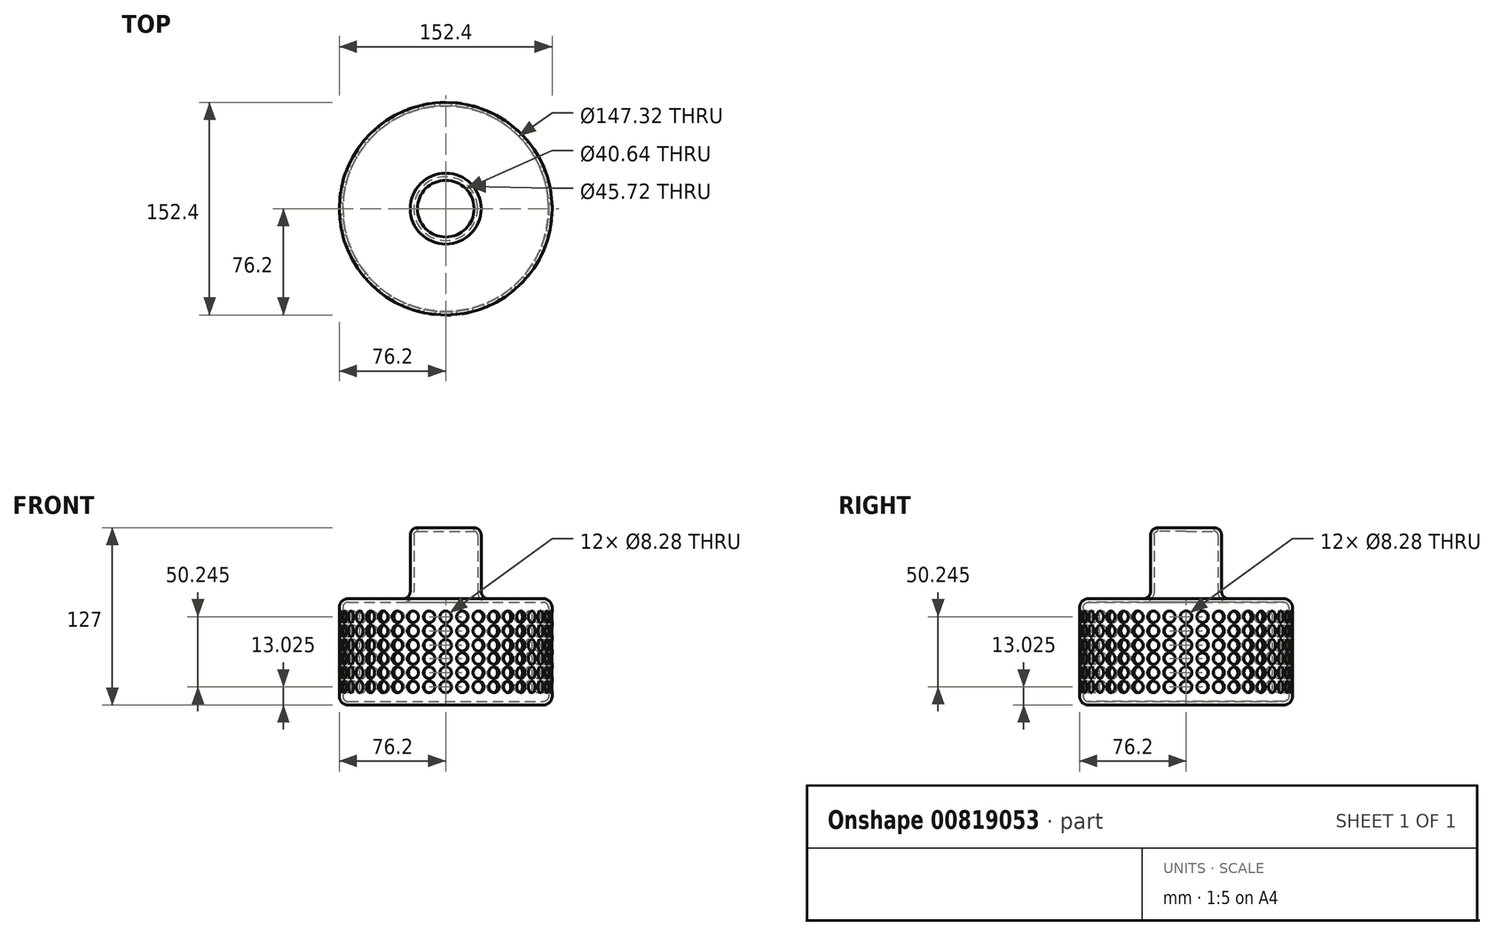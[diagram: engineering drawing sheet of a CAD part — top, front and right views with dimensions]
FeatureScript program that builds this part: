
annotation { "Feature Type Name" : "Feature", "Feature Type Description" : "" }
export const myFeature = defineFeature(function(context is Context, id is Id, definition is map)
    precondition{}
    {
        {
            var Q0;
            Q0=qCreatedBy(makeId("Front.planeOp"),FACE);
            var sketch = newSketch(context, id + "F0", { "sketchPlane" : qUnion([Q0])});
            skLineSegment(sketch, "E0.bottom", {"start": v(0, 0) * mm, "end": v(-69.85, 0) * mm});
            skLineSegment(sketch, "E0.top", {"start": v(0, 76.2) * mm, "end": v(-69.85, 76.2) * mm});
            skLineSegment(sketch, "E0.left", {"start": v(0, 0) * mm, "end": v(0, 76.2) * mm});
            skLineSegment(sketch, "E0.right", {"start": v(-76.2, 6.35) * mm, "end": v(-76.2, 69.85) * mm});
            skPoint(sketch, "E1.visualSharp", {"position": v(-76.2, 0) * mm});
            skArc(sketch, "E1.filletArc", {"start": v(-76.2, 6.35) * mm, "mid": v(-74.34, 1.86) * mm, "end": v(-69.85, 0) * mm});
            skPoint(sketch, "E2.visualSharp", {"position": v(-76.2, 76.2) * mm});
            skArc(sketch, "E2.filletArc", {"start": v(-69.85, 76.2) * mm, "mid": v(-74.34, 74.34) * mm, "end": v(-76.2, 69.85) * mm});
            skSolve(sketch);
        }
        {
            var Q0;
            Q0=makeQuery(id+"F0.imprint","IMPRINT",FACE,{"disambiguationData":[TD([[makeQuery(id+"F0.imprint","IMPRINT",EDGE,{"derivedFrom":sQuery(id+"F0.wireOp",EDGE,"E0.bottom")}),-1.0]])]});
            var Q1;
            Q1=sQuery(id+"F0.wireOp",EDGE,"E0.left");
            revolve(context, id + "F1", {"surfaceOperationType" : NewSurfaceOperationType.NEW, "entities" : qUnion([Q0]), "axis" : qUnion([Q1]), "revolveType" : RevolveType.FULL});
        }
        {
            var Q0;
            Q0=sQuery(id+"F0.wireOp",EDGE,"E0.right");
            cPlane(context, id + "F2", {"entities" : qUnion([Q0]), "cplaneType" : CPlaneType.LINE_ANGLE, "offset" : 25.4 * mm, "angle" : 0 * degree, "width" : 152.4 * mm, "height" : 152.4 * mm});
        }
        {
            var Q0;
            Q0=qCreatedBy(id+"F2.planeOp",FACE);
            var sketch = newSketch(context, id + "F3", { "sketchPlane" : qUnion([Q0])});
            skCircle(sketch, "E3", {"center": v(0, 63.27) * mm, "radius": 4.14 * mm});
            skCircle(sketch, "E4", {"center": v(0, 53.07) * mm, "radius": 4.14 * mm});
            skCircle(sketch, "E5", {"center": v(0, 42.83) * mm, "radius": 4.14 * mm});
            skCircle(sketch, "E6", {"center": v(0, 13.03) * mm, "radius": 4.14 * mm});
            skCircle(sketch, "E7", {"center": v(0, 23.2) * mm, "radius": 4.14 * mm});
            skCircle(sketch, "E8", {"center": v(0, 33.25) * mm, "radius": 4.14 * mm});
            skSolve(sketch);
        }
        {
            var Q0;
            Q0=makeQuery(id+"F1.opRevolve","SWEPT_FACE",FACE,{"disambiguationData":[OSD([sQuery(id+"F0.wireOp",EDGE,"E0.top")])]});
            var sketch = newSketch(context, id + "F4", { "sketchPlane" : qUnion([Q0])});
            skCircle(sketch, "E9", {"center": v(0, 0) * mm, "radius": 25.4 * mm});
            skSolve(sketch);
        }
        {
            var Q0;
            Q0=makeQuery(id+"F4.imprint","IMPRINT",FACE,{"disambiguationData":[TD([[makeQuery(id+"F4.imprint","IMPRINT",EDGE,{"derivedFrom":sQuery(id+"F4.wireOp",EDGE,"E9")}),1.0]])]});
            extrude(context, id + "F5", {"entities" : qUnion([Q0]), "operationType" : NewBodyOperationType.ADD, "depth" : 50.8 * mm, "offsetDistance" : 25.4 * mm});
        }
        {
            var Q0;
            Q0=makeQuery(id+"F1.opRevolve","SWEPT_FACE",FACE,{"disambiguationData":[OSD([sQuery(id+"F0.wireOp",EDGE,"E0.top")])]});
            var Q1;
            Q1=makeQuery(id+"F5.opExtrude","SWEPT_FACE",FACE,{"disambiguationData":[OSD([sQuery(id+"F4.wireOp",EDGE,"E9")])]});
            fillet(context, id + "F6", {"entities" : qUnion([Q0, Q1]), "radius" : 5.08 * mm, "tangentPropagation" : true, "allowEdgeOverflow" : false});
        }
        {
            var Q0;
            Q0=makeQuery(id+"F5.opExtrude","CAP_FACE",FACE,{"disambiguationData":[OSD([sQuery(id+"F4.wireOp",EDGE,"E9")])],"isStart":false});
            shell(context, id + "F7", {"entities" : qUnion([Q0]), "thickness" : 2.54 * mm});
        }
        {
            var Q0;
            Q0 = qSketchRegion(id + "F3", true);
            extrude(context, id + "F8", {"entities" : qUnion([Q0]), "operationType" : NewBodyOperationType.REMOVE, "depth" : 3.3 * mm, "offsetDistance" : 25.4 * mm});
        }
        {
            var Q0;
            Q0=makeQuery(id+"F1.opRevolve","SWEPT_BODY",BODY,{"disambiguationData":[OSD([sQuery(id+"F0.wireOp",EDGE,"E0.bottom"),sQuery(id+"F0.wireOp",EDGE,"E0.top"),sQuery(id+"F0.wireOp",EDGE,"E0.left"),sQuery(id+"F0.wireOp",EDGE,"E0.right"),sQuery(id+"F0.wireOp",EDGE,"E1.filletArc"),sQuery(id+"F0.wireOp",EDGE,"E2.filletArc")])]});
            var Q1;
            Q1=sQuery(id+"F0.wireOp",EDGE,"E0.left");
            circularPattern(context, id + "F9", {"entities" : qUnion([Q0]), "axis" : qUnion([Q1]), "angle" : 360 * degree, "instanceCount" : 40, "equalSpace" : true});
        }
        {
            var Q0;
            Q0=makeQuery(id+"F1.opRevolve","SWEPT_BODY",BODY,{"disambiguationData":[OSD([sQuery(id+"F0.wireOp",EDGE,"E0.bottom"),sQuery(id+"F0.wireOp",EDGE,"E0.top"),sQuery(id+"F0.wireOp",EDGE,"E0.left"),sQuery(id+"F0.wireOp",EDGE,"E0.right"),sQuery(id+"F0.wireOp",EDGE,"E1.filletArc"),sQuery(id+"F0.wireOp",EDGE,"E2.filletArc")])]});
            var Q1;
            Q1=makeQuery(id+"F9.opPattern","COPY",BODY,{"derivedFrom":makeQuery(id+"F1.opRevolve","SWEPT_BODY",BODY,{"disambiguationData":[OSD([sQuery(id+"F0.wireOp",EDGE,"E0.bottom"),sQuery(id+"F0.wireOp",EDGE,"E0.top"),sQuery(id+"F0.wireOp",EDGE,"E0.left"),sQuery(id+"F0.wireOp",EDGE,"E0.right"),sQuery(id+"F0.wireOp",EDGE,"E1.filletArc"),sQuery(id+"F0.wireOp",EDGE,"E2.filletArc")])]}),"instanceName":"1"});
            var Q2;
            Q2=makeQuery(id+"F9.opPattern","COPY",BODY,{"derivedFrom":makeQuery(id+"F1.opRevolve","SWEPT_BODY",BODY,{"disambiguationData":[OSD([sQuery(id+"F0.wireOp",EDGE,"E0.bottom"),sQuery(id+"F0.wireOp",EDGE,"E0.top"),sQuery(id+"F0.wireOp",EDGE,"E0.left"),sQuery(id+"F0.wireOp",EDGE,"E0.right"),sQuery(id+"F0.wireOp",EDGE,"E1.filletArc"),sQuery(id+"F0.wireOp",EDGE,"E2.filletArc")])]}),"instanceName":"2"});
            var Q3;
            Q3=makeQuery(id+"F9.opPattern","COPY",BODY,{"derivedFrom":makeQuery(id+"F1.opRevolve","SWEPT_BODY",BODY,{"disambiguationData":[OSD([sQuery(id+"F0.wireOp",EDGE,"E0.bottom"),sQuery(id+"F0.wireOp",EDGE,"E0.top"),sQuery(id+"F0.wireOp",EDGE,"E0.left"),sQuery(id+"F0.wireOp",EDGE,"E0.right"),sQuery(id+"F0.wireOp",EDGE,"E1.filletArc"),sQuery(id+"F0.wireOp",EDGE,"E2.filletArc")])]}),"instanceName":"3"});
            var Q4;
            Q4=makeQuery(id+"F9.opPattern","COPY",BODY,{"derivedFrom":makeQuery(id+"F1.opRevolve","SWEPT_BODY",BODY,{"disambiguationData":[OSD([sQuery(id+"F0.wireOp",EDGE,"E0.bottom"),sQuery(id+"F0.wireOp",EDGE,"E0.top"),sQuery(id+"F0.wireOp",EDGE,"E0.left"),sQuery(id+"F0.wireOp",EDGE,"E0.right"),sQuery(id+"F0.wireOp",EDGE,"E1.filletArc"),sQuery(id+"F0.wireOp",EDGE,"E2.filletArc")])]}),"instanceName":"4"});
            var Q5;
            Q5=makeQuery(id+"F9.opPattern","COPY",BODY,{"derivedFrom":makeQuery(id+"F1.opRevolve","SWEPT_BODY",BODY,{"disambiguationData":[OSD([sQuery(id+"F0.wireOp",EDGE,"E0.bottom"),sQuery(id+"F0.wireOp",EDGE,"E0.top"),sQuery(id+"F0.wireOp",EDGE,"E0.left"),sQuery(id+"F0.wireOp",EDGE,"E0.right"),sQuery(id+"F0.wireOp",EDGE,"E1.filletArc"),sQuery(id+"F0.wireOp",EDGE,"E2.filletArc")])]}),"instanceName":"5"});
            var Q6;
            Q6=makeQuery(id+"F9.opPattern","COPY",BODY,{"derivedFrom":makeQuery(id+"F1.opRevolve","SWEPT_BODY",BODY,{"disambiguationData":[OSD([sQuery(id+"F0.wireOp",EDGE,"E0.bottom"),sQuery(id+"F0.wireOp",EDGE,"E0.top"),sQuery(id+"F0.wireOp",EDGE,"E0.left"),sQuery(id+"F0.wireOp",EDGE,"E0.right"),sQuery(id+"F0.wireOp",EDGE,"E1.filletArc"),sQuery(id+"F0.wireOp",EDGE,"E2.filletArc")])]}),"instanceName":"6"});
            var Q7;
            Q7=makeQuery(id+"F9.opPattern","COPY",BODY,{"derivedFrom":makeQuery(id+"F1.opRevolve","SWEPT_BODY",BODY,{"disambiguationData":[OSD([sQuery(id+"F0.wireOp",EDGE,"E0.bottom"),sQuery(id+"F0.wireOp",EDGE,"E0.top"),sQuery(id+"F0.wireOp",EDGE,"E0.left"),sQuery(id+"F0.wireOp",EDGE,"E0.right"),sQuery(id+"F0.wireOp",EDGE,"E1.filletArc"),sQuery(id+"F0.wireOp",EDGE,"E2.filletArc")])]}),"instanceName":"7"});
            var Q8;
            Q8=makeQuery(id+"F9.opPattern","COPY",BODY,{"derivedFrom":makeQuery(id+"F1.opRevolve","SWEPT_BODY",BODY,{"disambiguationData":[OSD([sQuery(id+"F0.wireOp",EDGE,"E0.bottom"),sQuery(id+"F0.wireOp",EDGE,"E0.top"),sQuery(id+"F0.wireOp",EDGE,"E0.left"),sQuery(id+"F0.wireOp",EDGE,"E0.right"),sQuery(id+"F0.wireOp",EDGE,"E1.filletArc"),sQuery(id+"F0.wireOp",EDGE,"E2.filletArc")])]}),"instanceName":"8"});
            var Q9;
            Q9=makeQuery(id+"F9.opPattern","COPY",BODY,{"derivedFrom":makeQuery(id+"F1.opRevolve","SWEPT_BODY",BODY,{"disambiguationData":[OSD([sQuery(id+"F0.wireOp",EDGE,"E0.bottom"),sQuery(id+"F0.wireOp",EDGE,"E0.top"),sQuery(id+"F0.wireOp",EDGE,"E0.left"),sQuery(id+"F0.wireOp",EDGE,"E0.right"),sQuery(id+"F0.wireOp",EDGE,"E1.filletArc"),sQuery(id+"F0.wireOp",EDGE,"E2.filletArc")])]}),"instanceName":"9"});
            var Q10;
            Q10=makeQuery(id+"F9.opPattern","COPY",BODY,{"derivedFrom":makeQuery(id+"F1.opRevolve","SWEPT_BODY",BODY,{"disambiguationData":[OSD([sQuery(id+"F0.wireOp",EDGE,"E0.bottom"),sQuery(id+"F0.wireOp",EDGE,"E0.top"),sQuery(id+"F0.wireOp",EDGE,"E0.left"),sQuery(id+"F0.wireOp",EDGE,"E0.right"),sQuery(id+"F0.wireOp",EDGE,"E1.filletArc"),sQuery(id+"F0.wireOp",EDGE,"E2.filletArc")])]}),"instanceName":"10"});
            var Q11;
            Q11=makeQuery(id+"F9.opPattern","COPY",BODY,{"derivedFrom":makeQuery(id+"F1.opRevolve","SWEPT_BODY",BODY,{"disambiguationData":[OSD([sQuery(id+"F0.wireOp",EDGE,"E0.bottom"),sQuery(id+"F0.wireOp",EDGE,"E0.top"),sQuery(id+"F0.wireOp",EDGE,"E0.left"),sQuery(id+"F0.wireOp",EDGE,"E0.right"),sQuery(id+"F0.wireOp",EDGE,"E1.filletArc"),sQuery(id+"F0.wireOp",EDGE,"E2.filletArc")])]}),"instanceName":"11"});
            var Q12;
            Q12=makeQuery(id+"F9.opPattern","COPY",BODY,{"derivedFrom":makeQuery(id+"F1.opRevolve","SWEPT_BODY",BODY,{"disambiguationData":[OSD([sQuery(id+"F0.wireOp",EDGE,"E0.bottom"),sQuery(id+"F0.wireOp",EDGE,"E0.top"),sQuery(id+"F0.wireOp",EDGE,"E0.left"),sQuery(id+"F0.wireOp",EDGE,"E0.right"),sQuery(id+"F0.wireOp",EDGE,"E1.filletArc"),sQuery(id+"F0.wireOp",EDGE,"E2.filletArc")])]}),"instanceName":"12"});
            var Q13;
            Q13=makeQuery(id+"F9.opPattern","COPY",BODY,{"derivedFrom":makeQuery(id+"F1.opRevolve","SWEPT_BODY",BODY,{"disambiguationData":[OSD([sQuery(id+"F0.wireOp",EDGE,"E0.bottom"),sQuery(id+"F0.wireOp",EDGE,"E0.top"),sQuery(id+"F0.wireOp",EDGE,"E0.left"),sQuery(id+"F0.wireOp",EDGE,"E0.right"),sQuery(id+"F0.wireOp",EDGE,"E1.filletArc"),sQuery(id+"F0.wireOp",EDGE,"E2.filletArc")])]}),"instanceName":"13"});
            var Q14;
            Q14=makeQuery(id+"F9.opPattern","COPY",BODY,{"derivedFrom":makeQuery(id+"F1.opRevolve","SWEPT_BODY",BODY,{"disambiguationData":[OSD([sQuery(id+"F0.wireOp",EDGE,"E0.bottom"),sQuery(id+"F0.wireOp",EDGE,"E0.top"),sQuery(id+"F0.wireOp",EDGE,"E0.left"),sQuery(id+"F0.wireOp",EDGE,"E0.right"),sQuery(id+"F0.wireOp",EDGE,"E1.filletArc"),sQuery(id+"F0.wireOp",EDGE,"E2.filletArc")])]}),"instanceName":"14"});
            var Q15;
            Q15=makeQuery(id+"F9.opPattern","COPY",BODY,{"derivedFrom":makeQuery(id+"F1.opRevolve","SWEPT_BODY",BODY,{"disambiguationData":[OSD([sQuery(id+"F0.wireOp",EDGE,"E0.bottom"),sQuery(id+"F0.wireOp",EDGE,"E0.top"),sQuery(id+"F0.wireOp",EDGE,"E0.left"),sQuery(id+"F0.wireOp",EDGE,"E0.right"),sQuery(id+"F0.wireOp",EDGE,"E1.filletArc"),sQuery(id+"F0.wireOp",EDGE,"E2.filletArc")])]}),"instanceName":"15"});
            var Q16;
            Q16=makeQuery(id+"F9.opPattern","COPY",BODY,{"derivedFrom":makeQuery(id+"F1.opRevolve","SWEPT_BODY",BODY,{"disambiguationData":[OSD([sQuery(id+"F0.wireOp",EDGE,"E0.bottom"),sQuery(id+"F0.wireOp",EDGE,"E0.top"),sQuery(id+"F0.wireOp",EDGE,"E0.left"),sQuery(id+"F0.wireOp",EDGE,"E0.right"),sQuery(id+"F0.wireOp",EDGE,"E1.filletArc"),sQuery(id+"F0.wireOp",EDGE,"E2.filletArc")])]}),"instanceName":"16"});
            var Q17;
            Q17=makeQuery(id+"F9.opPattern","COPY",BODY,{"derivedFrom":makeQuery(id+"F1.opRevolve","SWEPT_BODY",BODY,{"disambiguationData":[OSD([sQuery(id+"F0.wireOp",EDGE,"E0.bottom"),sQuery(id+"F0.wireOp",EDGE,"E0.top"),sQuery(id+"F0.wireOp",EDGE,"E0.left"),sQuery(id+"F0.wireOp",EDGE,"E0.right"),sQuery(id+"F0.wireOp",EDGE,"E1.filletArc"),sQuery(id+"F0.wireOp",EDGE,"E2.filletArc")])]}),"instanceName":"17"});
            var Q18;
            Q18=makeQuery(id+"F9.opPattern","COPY",BODY,{"derivedFrom":makeQuery(id+"F1.opRevolve","SWEPT_BODY",BODY,{"disambiguationData":[OSD([sQuery(id+"F0.wireOp",EDGE,"E0.bottom"),sQuery(id+"F0.wireOp",EDGE,"E0.top"),sQuery(id+"F0.wireOp",EDGE,"E0.left"),sQuery(id+"F0.wireOp",EDGE,"E0.right"),sQuery(id+"F0.wireOp",EDGE,"E1.filletArc"),sQuery(id+"F0.wireOp",EDGE,"E2.filletArc")])]}),"instanceName":"18"});
            var Q19;
            Q19=makeQuery(id+"F9.opPattern","COPY",BODY,{"derivedFrom":makeQuery(id+"F1.opRevolve","SWEPT_BODY",BODY,{"disambiguationData":[OSD([sQuery(id+"F0.wireOp",EDGE,"E0.bottom"),sQuery(id+"F0.wireOp",EDGE,"E0.top"),sQuery(id+"F0.wireOp",EDGE,"E0.left"),sQuery(id+"F0.wireOp",EDGE,"E0.right"),sQuery(id+"F0.wireOp",EDGE,"E1.filletArc"),sQuery(id+"F0.wireOp",EDGE,"E2.filletArc")])]}),"instanceName":"19"});
            var Q20;
            Q20=makeQuery(id+"F9.opPattern","COPY",BODY,{"derivedFrom":makeQuery(id+"F1.opRevolve","SWEPT_BODY",BODY,{"disambiguationData":[OSD([sQuery(id+"F0.wireOp",EDGE,"E0.bottom"),sQuery(id+"F0.wireOp",EDGE,"E0.top"),sQuery(id+"F0.wireOp",EDGE,"E0.left"),sQuery(id+"F0.wireOp",EDGE,"E0.right"),sQuery(id+"F0.wireOp",EDGE,"E1.filletArc"),sQuery(id+"F0.wireOp",EDGE,"E2.filletArc")])]}),"instanceName":"20"});
            var Q21;
            Q21=makeQuery(id+"F9.opPattern","COPY",BODY,{"derivedFrom":makeQuery(id+"F1.opRevolve","SWEPT_BODY",BODY,{"disambiguationData":[OSD([sQuery(id+"F0.wireOp",EDGE,"E0.bottom"),sQuery(id+"F0.wireOp",EDGE,"E0.top"),sQuery(id+"F0.wireOp",EDGE,"E0.left"),sQuery(id+"F0.wireOp",EDGE,"E0.right"),sQuery(id+"F0.wireOp",EDGE,"E1.filletArc"),sQuery(id+"F0.wireOp",EDGE,"E2.filletArc")])]}),"instanceName":"21"});
            var Q22;
            Q22=makeQuery(id+"F9.opPattern","COPY",BODY,{"derivedFrom":makeQuery(id+"F1.opRevolve","SWEPT_BODY",BODY,{"disambiguationData":[OSD([sQuery(id+"F0.wireOp",EDGE,"E0.bottom"),sQuery(id+"F0.wireOp",EDGE,"E0.top"),sQuery(id+"F0.wireOp",EDGE,"E0.left"),sQuery(id+"F0.wireOp",EDGE,"E0.right"),sQuery(id+"F0.wireOp",EDGE,"E1.filletArc"),sQuery(id+"F0.wireOp",EDGE,"E2.filletArc")])]}),"instanceName":"22"});
            var Q23;
            Q23=makeQuery(id+"F9.opPattern","COPY",BODY,{"derivedFrom":makeQuery(id+"F1.opRevolve","SWEPT_BODY",BODY,{"disambiguationData":[OSD([sQuery(id+"F0.wireOp",EDGE,"E0.bottom"),sQuery(id+"F0.wireOp",EDGE,"E0.top"),sQuery(id+"F0.wireOp",EDGE,"E0.left"),sQuery(id+"F0.wireOp",EDGE,"E0.right"),sQuery(id+"F0.wireOp",EDGE,"E1.filletArc"),sQuery(id+"F0.wireOp",EDGE,"E2.filletArc")])]}),"instanceName":"23"});
            var Q24;
            Q24=makeQuery(id+"F9.opPattern","COPY",BODY,{"derivedFrom":makeQuery(id+"F1.opRevolve","SWEPT_BODY",BODY,{"disambiguationData":[OSD([sQuery(id+"F0.wireOp",EDGE,"E0.bottom"),sQuery(id+"F0.wireOp",EDGE,"E0.top"),sQuery(id+"F0.wireOp",EDGE,"E0.left"),sQuery(id+"F0.wireOp",EDGE,"E0.right"),sQuery(id+"F0.wireOp",EDGE,"E1.filletArc"),sQuery(id+"F0.wireOp",EDGE,"E2.filletArc")])]}),"instanceName":"24"});
            var Q25;
            Q25=makeQuery(id+"F9.opPattern","COPY",BODY,{"derivedFrom":makeQuery(id+"F1.opRevolve","SWEPT_BODY",BODY,{"disambiguationData":[OSD([sQuery(id+"F0.wireOp",EDGE,"E0.bottom"),sQuery(id+"F0.wireOp",EDGE,"E0.top"),sQuery(id+"F0.wireOp",EDGE,"E0.left"),sQuery(id+"F0.wireOp",EDGE,"E0.right"),sQuery(id+"F0.wireOp",EDGE,"E1.filletArc"),sQuery(id+"F0.wireOp",EDGE,"E2.filletArc")])]}),"instanceName":"25"});
            var Q26;
            Q26=makeQuery(id+"F9.opPattern","COPY",BODY,{"derivedFrom":makeQuery(id+"F1.opRevolve","SWEPT_BODY",BODY,{"disambiguationData":[OSD([sQuery(id+"F0.wireOp",EDGE,"E0.bottom"),sQuery(id+"F0.wireOp",EDGE,"E0.top"),sQuery(id+"F0.wireOp",EDGE,"E0.left"),sQuery(id+"F0.wireOp",EDGE,"E0.right"),sQuery(id+"F0.wireOp",EDGE,"E1.filletArc"),sQuery(id+"F0.wireOp",EDGE,"E2.filletArc")])]}),"instanceName":"26"});
            var Q27;
            Q27=makeQuery(id+"F9.opPattern","COPY",BODY,{"derivedFrom":makeQuery(id+"F1.opRevolve","SWEPT_BODY",BODY,{"disambiguationData":[OSD([sQuery(id+"F0.wireOp",EDGE,"E0.bottom"),sQuery(id+"F0.wireOp",EDGE,"E0.top"),sQuery(id+"F0.wireOp",EDGE,"E0.left"),sQuery(id+"F0.wireOp",EDGE,"E0.right"),sQuery(id+"F0.wireOp",EDGE,"E1.filletArc"),sQuery(id+"F0.wireOp",EDGE,"E2.filletArc")])]}),"instanceName":"27"});
            var Q28;
            Q28=makeQuery(id+"F9.opPattern","COPY",BODY,{"derivedFrom":makeQuery(id+"F1.opRevolve","SWEPT_BODY",BODY,{"disambiguationData":[OSD([sQuery(id+"F0.wireOp",EDGE,"E0.bottom"),sQuery(id+"F0.wireOp",EDGE,"E0.top"),sQuery(id+"F0.wireOp",EDGE,"E0.left"),sQuery(id+"F0.wireOp",EDGE,"E0.right"),sQuery(id+"F0.wireOp",EDGE,"E1.filletArc"),sQuery(id+"F0.wireOp",EDGE,"E2.filletArc")])]}),"instanceName":"28"});
            var Q29;
            Q29=makeQuery(id+"F9.opPattern","COPY",BODY,{"derivedFrom":makeQuery(id+"F1.opRevolve","SWEPT_BODY",BODY,{"disambiguationData":[OSD([sQuery(id+"F0.wireOp",EDGE,"E0.bottom"),sQuery(id+"F0.wireOp",EDGE,"E0.top"),sQuery(id+"F0.wireOp",EDGE,"E0.left"),sQuery(id+"F0.wireOp",EDGE,"E0.right"),sQuery(id+"F0.wireOp",EDGE,"E1.filletArc"),sQuery(id+"F0.wireOp",EDGE,"E2.filletArc")])]}),"instanceName":"29"});
            var Q30;
            Q30=makeQuery(id+"F9.opPattern","COPY",BODY,{"derivedFrom":makeQuery(id+"F1.opRevolve","SWEPT_BODY",BODY,{"disambiguationData":[OSD([sQuery(id+"F0.wireOp",EDGE,"E0.bottom"),sQuery(id+"F0.wireOp",EDGE,"E0.top"),sQuery(id+"F0.wireOp",EDGE,"E0.left"),sQuery(id+"F0.wireOp",EDGE,"E0.right"),sQuery(id+"F0.wireOp",EDGE,"E1.filletArc"),sQuery(id+"F0.wireOp",EDGE,"E2.filletArc")])]}),"instanceName":"30"});
            var Q31;
            Q31=makeQuery(id+"F9.opPattern","COPY",BODY,{"derivedFrom":makeQuery(id+"F1.opRevolve","SWEPT_BODY",BODY,{"disambiguationData":[OSD([sQuery(id+"F0.wireOp",EDGE,"E0.bottom"),sQuery(id+"F0.wireOp",EDGE,"E0.top"),sQuery(id+"F0.wireOp",EDGE,"E0.left"),sQuery(id+"F0.wireOp",EDGE,"E0.right"),sQuery(id+"F0.wireOp",EDGE,"E1.filletArc"),sQuery(id+"F0.wireOp",EDGE,"E2.filletArc")])]}),"instanceName":"31"});
            var Q32;
            Q32=makeQuery(id+"F9.opPattern","COPY",BODY,{"derivedFrom":makeQuery(id+"F1.opRevolve","SWEPT_BODY",BODY,{"disambiguationData":[OSD([sQuery(id+"F0.wireOp",EDGE,"E0.bottom"),sQuery(id+"F0.wireOp",EDGE,"E0.top"),sQuery(id+"F0.wireOp",EDGE,"E0.left"),sQuery(id+"F0.wireOp",EDGE,"E0.right"),sQuery(id+"F0.wireOp",EDGE,"E1.filletArc"),sQuery(id+"F0.wireOp",EDGE,"E2.filletArc")])]}),"instanceName":"32"});
            var Q33;
            Q33=makeQuery(id+"F9.opPattern","COPY",BODY,{"derivedFrom":makeQuery(id+"F1.opRevolve","SWEPT_BODY",BODY,{"disambiguationData":[OSD([sQuery(id+"F0.wireOp",EDGE,"E0.bottom"),sQuery(id+"F0.wireOp",EDGE,"E0.top"),sQuery(id+"F0.wireOp",EDGE,"E0.left"),sQuery(id+"F0.wireOp",EDGE,"E0.right"),sQuery(id+"F0.wireOp",EDGE,"E1.filletArc"),sQuery(id+"F0.wireOp",EDGE,"E2.filletArc")])]}),"instanceName":"33"});
            var Q34;
            Q34=makeQuery(id+"F9.opPattern","COPY",BODY,{"derivedFrom":makeQuery(id+"F1.opRevolve","SWEPT_BODY",BODY,{"disambiguationData":[OSD([sQuery(id+"F0.wireOp",EDGE,"E0.bottom"),sQuery(id+"F0.wireOp",EDGE,"E0.top"),sQuery(id+"F0.wireOp",EDGE,"E0.left"),sQuery(id+"F0.wireOp",EDGE,"E0.right"),sQuery(id+"F0.wireOp",EDGE,"E1.filletArc"),sQuery(id+"F0.wireOp",EDGE,"E2.filletArc")])]}),"instanceName":"34"});
            var Q35;
            Q35=makeQuery(id+"F9.opPattern","COPY",BODY,{"derivedFrom":makeQuery(id+"F1.opRevolve","SWEPT_BODY",BODY,{"disambiguationData":[OSD([sQuery(id+"F0.wireOp",EDGE,"E0.bottom"),sQuery(id+"F0.wireOp",EDGE,"E0.top"),sQuery(id+"F0.wireOp",EDGE,"E0.left"),sQuery(id+"F0.wireOp",EDGE,"E0.right"),sQuery(id+"F0.wireOp",EDGE,"E1.filletArc"),sQuery(id+"F0.wireOp",EDGE,"E2.filletArc")])]}),"instanceName":"35"});
            var Q36;
            Q36=makeQuery(id+"F9.opPattern","COPY",BODY,{"derivedFrom":makeQuery(id+"F1.opRevolve","SWEPT_BODY",BODY,{"disambiguationData":[OSD([sQuery(id+"F0.wireOp",EDGE,"E0.bottom"),sQuery(id+"F0.wireOp",EDGE,"E0.top"),sQuery(id+"F0.wireOp",EDGE,"E0.left"),sQuery(id+"F0.wireOp",EDGE,"E0.right"),sQuery(id+"F0.wireOp",EDGE,"E1.filletArc"),sQuery(id+"F0.wireOp",EDGE,"E2.filletArc")])]}),"instanceName":"36"});
            var Q37;
            Q37=makeQuery(id+"F9.opPattern","COPY",BODY,{"derivedFrom":makeQuery(id+"F1.opRevolve","SWEPT_BODY",BODY,{"disambiguationData":[OSD([sQuery(id+"F0.wireOp",EDGE,"E0.bottom"),sQuery(id+"F0.wireOp",EDGE,"E0.top"),sQuery(id+"F0.wireOp",EDGE,"E0.left"),sQuery(id+"F0.wireOp",EDGE,"E0.right"),sQuery(id+"F0.wireOp",EDGE,"E1.filletArc"),sQuery(id+"F0.wireOp",EDGE,"E2.filletArc")])]}),"instanceName":"37"});
            var Q38;
            Q38=makeQuery(id+"F9.opPattern","COPY",BODY,{"derivedFrom":makeQuery(id+"F1.opRevolve","SWEPT_BODY",BODY,{"disambiguationData":[OSD([sQuery(id+"F0.wireOp",EDGE,"E0.bottom"),sQuery(id+"F0.wireOp",EDGE,"E0.top"),sQuery(id+"F0.wireOp",EDGE,"E0.left"),sQuery(id+"F0.wireOp",EDGE,"E0.right"),sQuery(id+"F0.wireOp",EDGE,"E1.filletArc"),sQuery(id+"F0.wireOp",EDGE,"E2.filletArc")])]}),"instanceName":"38"});
            var Q39;
            Q39=makeQuery(id+"F9.opPattern","COPY",BODY,{"derivedFrom":makeQuery(id+"F1.opRevolve","SWEPT_BODY",BODY,{"disambiguationData":[OSD([sQuery(id+"F0.wireOp",EDGE,"E0.bottom"),sQuery(id+"F0.wireOp",EDGE,"E0.top"),sQuery(id+"F0.wireOp",EDGE,"E0.left"),sQuery(id+"F0.wireOp",EDGE,"E0.right"),sQuery(id+"F0.wireOp",EDGE,"E1.filletArc"),sQuery(id+"F0.wireOp",EDGE,"E2.filletArc")])]}),"instanceName":"39"});
            booleanBodies(context, id + "F10", {"operationType" : BooleanOperationType.INTERSECTION, "tools" : qUnion([Q0, Q1, Q2, Q3, Q4, Q5, Q6, Q7, Q8, Q9, Q10, Q11, Q12, Q13, Q14, Q15, Q16, Q17, Q18, Q19, Q20, Q21, Q22, Q23, Q24, Q25, Q26, Q27, Q28, Q29, Q30, Q31, Q32, Q33, Q34, Q35, Q36, Q37, Q38, Q39])});
        }
    });
